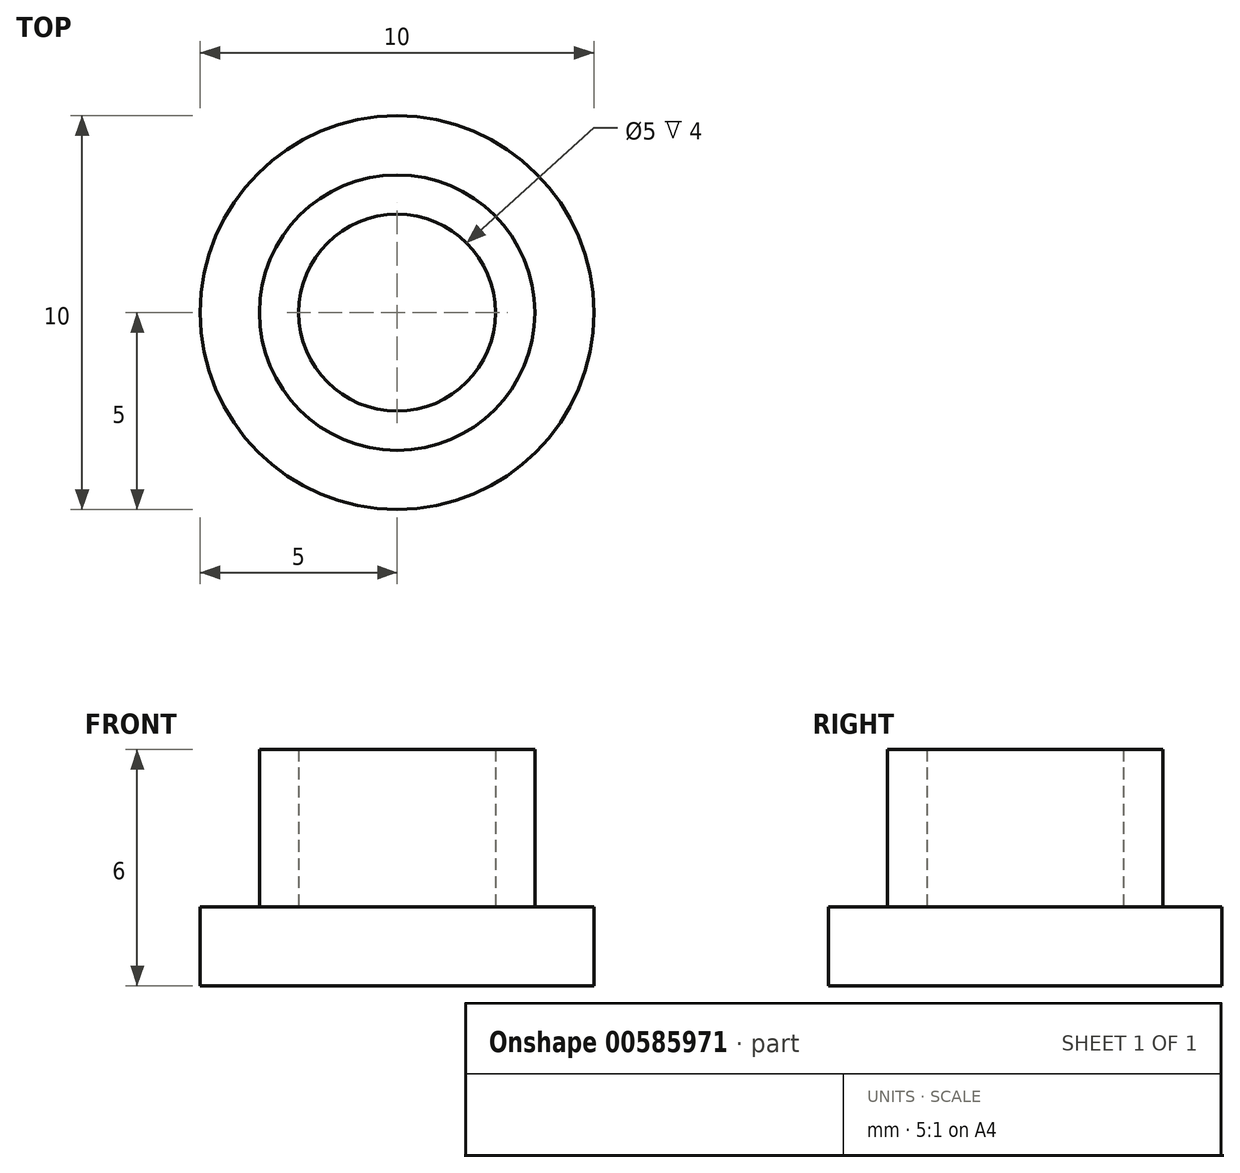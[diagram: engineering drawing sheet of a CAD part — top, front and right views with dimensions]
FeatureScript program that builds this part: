
annotation { "Feature Type Name" : "Feature", "Feature Type Description" : "" }
export const myFeature = defineFeature(function(context is Context, id is Id, definition is map)
    precondition{}
    {
        {
            var Q0;
            Q0=qCreatedBy(makeId("Top.planeOp"),FACE);
            var sketch = newSketch(context, id + "F0", { "sketchPlane" : qUnion([Q0])});
            skCircle(sketch, "E0", {"center": v(0, 0) * mm, "radius": 5 * mm});
            skCircle(sketch, "E1", {"center": v(0, 0) * mm, "radius": 2.5 * mm});
            skCircle(sketch, "E2", {"center": v(0, 0) * mm, "radius": 3.5 * mm});
            skSolve(sketch);
        }
        {
            var Q0;
            Q0=makeQuery(id+"F0.imprint","IMPRINT",FACE,{"disambiguationData":[TD([[makeQuery(id+"F0.imprint","IMPRINT",EDGE,{"derivedFrom":sQuery(id+"F0.wireOp",EDGE,"E0")}),1.0]])]});
            var Q1;
            Q1=makeQuery(id+"F0.imprint","IMPRINT",FACE,{"disambiguationData":[TD([[makeQuery(id+"F0.imprint","IMPRINT",EDGE,{"derivedFrom":sQuery(id+"F0.wireOp",EDGE,"E1")}),-1.0]])]});
            var Q2;
            Q2=makeQuery(id+"F0.imprint","IMPRINT",FACE,{"disambiguationData":[TD([[makeQuery(id+"F0.imprint","IMPRINT",EDGE,{"derivedFrom":sQuery(id+"F0.wireOp",EDGE,"E1")}),1.0]])]});
            extrude(context, id + "F1", {"entities" : qUnion([Q0, Q1, Q2]), "depth" : 2 * mm, "offsetDistance" : 25 * mm});
        }
        {
            var Q0;
            Q0=makeQuery(id+"F0.imprint","IMPRINT",FACE,{"disambiguationData":[TD([[makeQuery(id+"F0.imprint","IMPRINT",EDGE,{"derivedFrom":sQuery(id+"F0.wireOp",EDGE,"E1")}),-1.0]])]});
            extrude(context, id + "F2", {"entities" : qUnion([Q0]), "operationType" : NewBodyOperationType.ADD, "depth" : 6 * mm, "offsetDistance" : 25 * mm});
        }
    });
